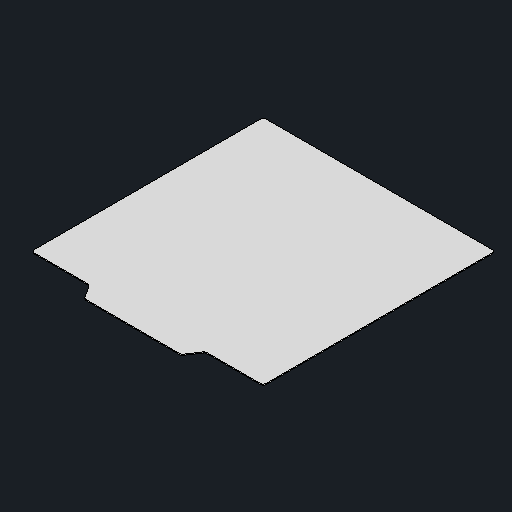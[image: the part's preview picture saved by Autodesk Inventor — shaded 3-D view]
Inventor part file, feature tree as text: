
AUTODESK INVENTOR PART (.ipt)
format: ipt  version: 2024.2 (Build 282272000, 272)  size: 80,384 bytes
history: native  units: mm
features: other x1, fillet x1
ambient origin geometry x8: Origin, YZ Plane, XZ Plane, XY Plane, X Axis, Y Axis, Z Axis, Center Point
bodies: Body1 (feature_tree)
feature tree (2):
  other  "솔리드1"
  fillet  "Fillet1"  [1 undecoded]
note: 1 required parameter value undecoded (feature->parameter linkage not recoverable at this tier; creation-order binding heuristic only, values carry confidence <= 0.55)
